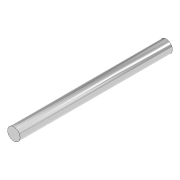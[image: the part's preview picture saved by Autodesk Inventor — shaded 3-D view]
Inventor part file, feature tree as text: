
AUTODESK INVENTOR PART (.ipt)
format: ipt  version: 2020 (Build 240168000, 168)  size: 78,848 bytes
history: native  units: in
note: dims shown in document units (in); Inventor stores cm internally (conversion verified against a paired STEP export)
features: extrude x1, sketch x1
ambient origin geometry x8: Origin, YZ Plane, XZ Plane, XY Plane, X Axis, Y Axis, Z Axis, Center Point
bodies: Solid1 (feature_tree)
feature tree (2):
  extrude  "Extrusion1"  Depth=2.4213in TaperAngle=0.0deg
  sketch  "Sketch1"  dims[d0=0.1969in d1=2.4213in d2=0.0in]
